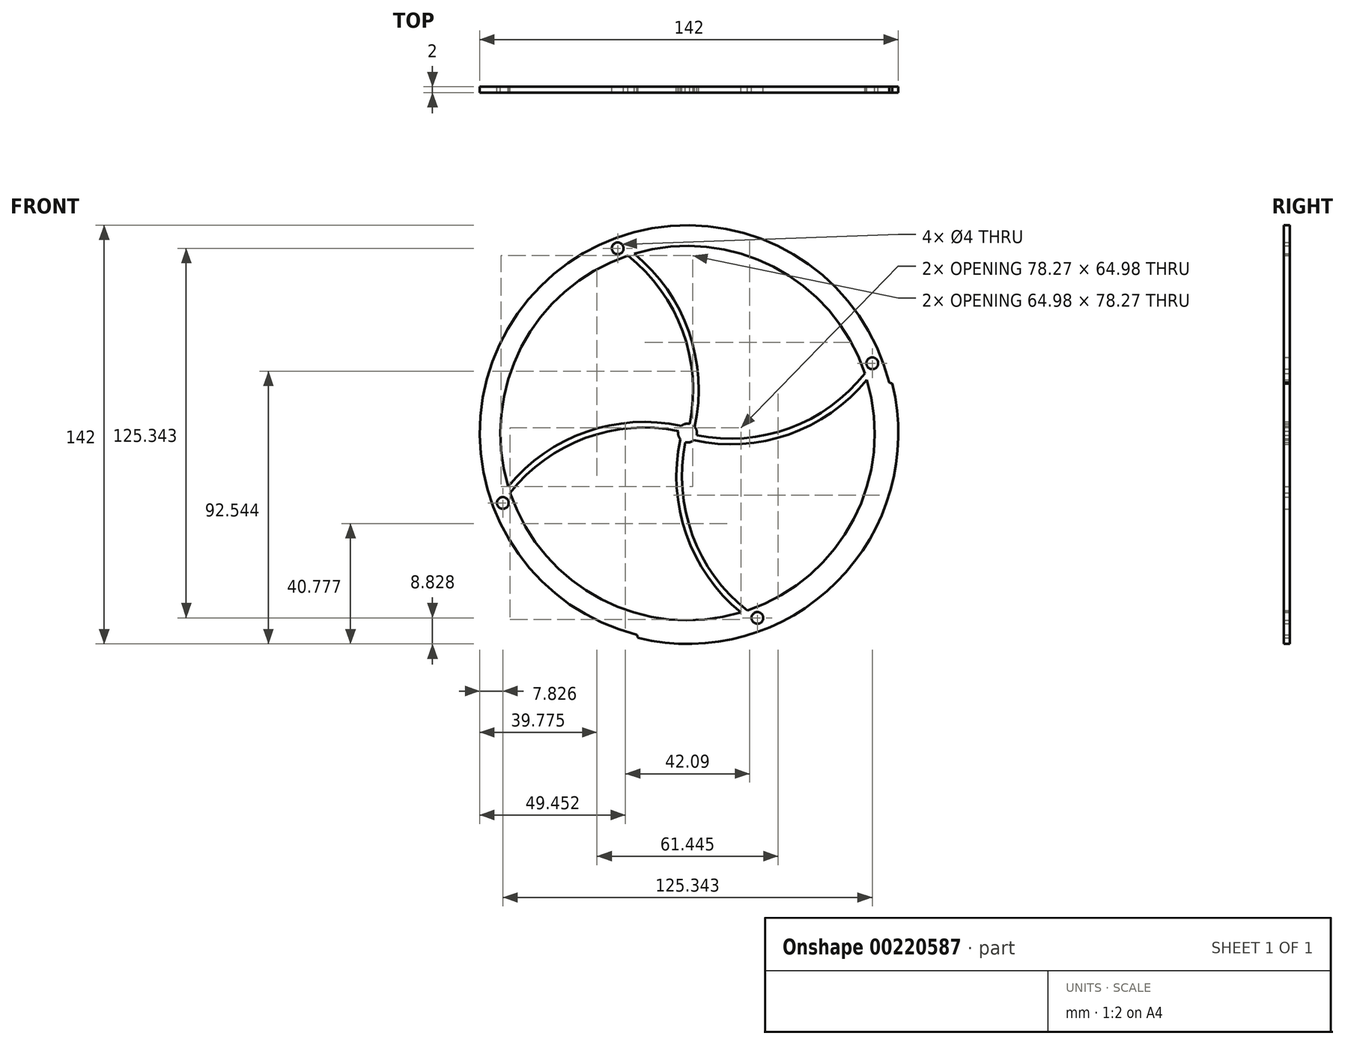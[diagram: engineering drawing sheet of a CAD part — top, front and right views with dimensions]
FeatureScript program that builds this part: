
annotation { "Feature Type Name" : "Feature", "Feature Type Description" : "" }
export const myFeature = defineFeature(function(context is Context, id is Id, definition is map)
    precondition{}
    {
        {
            var Q0;
            Q0=qCreatedBy(makeId("Front.planeOp"),FACE);
            var sketch = newSketch(context, id + "F0", { "sketchPlane" : qUnion([Q0])});
            skLineSegment(sketch, "E0.bottom", {"start": v(89.93, -111.44) * mm, "end": v(-110.07, -111.44) * mm});
            skLineSegment(sketch, "E0.top", {"start": v(89.93, 88.56) * mm, "end": v(-110.07, 88.56) * mm});
            skLineSegment(sketch, "E0.left", {"start": v(89.93, -111.44) * mm, "end": v(89.93, 88.56) * mm});
            skLineSegment(sketch, "E0.right", {"start": v(-110.07, -111.44) * mm, "end": v(-110.07, 88.56) * mm});
            skPoint(sketch, "E0.middle", {"position": v(-10.07, -11.44) * mm});
            skLineSegment(sketch, "E1", {"start": v(-110.07, 88.56) * mm, "end": v(89.93, -111.44) * mm, "construction": true});
            skLineSegment(sketch, "E2", {"start": v(89.93, 88.56) * mm, "end": v(-110.07, -111.44) * mm, "construction": true});
            skCircle(sketch, "E3", {"center": v(38.43, -59.95) * mm, "radius": 68.6 * mm});
            skCircle(sketch, "E4", {"center": v(38.6, 37.24) * mm, "radius": 68.84 * mm});
            skCircle(sketch, "E5", {"center": v(-16.12, 66.58) * mm, "radius": 6.75 * mm});
            skCircle(sketch, "E6", {"center": v(-10.07, -11.44) * mm, "radius": 71.5 * mm});
            skCircle(sketch, "E7", {"center": v(-16.12, 66.58) * mm, "radius": 2.5 * mm});
            skCircle(sketch, "E8", {"center": v(52.6, 12.25) * mm, "radius": 2.5 * mm});
            skCircle(sketch, "E9", {"center": v(62.37, 19.29) * mm, "radius": 2.5 * mm});
            skLineSegment(sketch, "E10", {"start": v(52.6, 12.25) * mm, "end": v(-33.76, 51.23) * mm, "construction": true});
            skLineSegment(sketch, "E11", {"start": v(-33.76, 51.23) * mm, "end": v(-72.74, -35.13) * mm, "construction": true});
            skLineSegment(sketch, "E12", {"start": v(-72.74, -35.13) * mm, "end": v(13.62, -74.11) * mm, "construction": true});
            skLineSegment(sketch, "E13", {"start": v(13.62, -74.11) * mm, "end": v(52.6, 12.25) * mm, "construction": true});
            skCircle(sketch, "E14", {"center": v(-10.07, -11.44) * mm, "radius": 67 * mm, "construction": true});
            skCircle(sketch, "E15", {"center": v(62.37, 19.29) * mm, "radius": 6.75 * mm, "construction": true});
            skArc(sketch, "E16", {"start": v(62.37, 19.29) * mm, "mid": v(30.57, 55.29) * mm, "end": v(-16.12, 66.58) * mm, "construction": true});
            skArc(sketch, "E17", {"start": v(60.01, 18.48) * mm, "mid": v(29.1, 53.19) * mm, "end": v(-16.1, 64.08) * mm});
            skArc(sketch, "E18", {"start": v(64.71, 20.17) * mm, "mid": v(31.98, 57.24) * mm, "end": v(-16.04, 69.07) * mm});
            skCircle(sketch, "E19", {"center": v(-33.76, 51.23) * mm, "radius": 2 * mm});
            skCircle(sketch, "E20", {"center": v(-72.74, -35.13) * mm, "radius": 2 * mm});
            skCircle(sketch, "E21", {"center": v(13.62, -74.11) * mm, "radius": 2 * mm});
            skCircle(sketch, "E22", {"center": v(52.6, 12.25) * mm, "radius": 2 * mm});
            skCircle(sketch, "E23", {"center": v(62.37, 19.29) * mm, "radius": 2 * mm});
            skCircle(sketch, "E24", {"center": v(-16.12, 66.58) * mm, "radius": 2 * mm});
            skArc(sketch, "E25", {"start": v(-10.07, -11.44) * mm, "mid": v(25.04, -9.58) * mm, "end": v(52.6, 12.25) * mm});
            skArc(sketch, "E26.0", {"start": v(-10.55, -13.28) * mm, "mid": v(25.7, -11.36) * mm, "end": v(54.17, 11.2) * mm});
            skLineSegment(sketch, "E27", {"start": v(-10.55, -13.28) * mm, "end": v(-10.07, -11.44) * mm});
            skLineSegment(sketch, "E28", {"start": v(52.6, 12.25) * mm, "end": v(54.17, 11.2) * mm});
            skArc(sketch, "E29.1.0", {"start": v(-8.23, -11.92) * mm, "mid": v(-10.15, 24.34) * mm, "end": v(-32.7, 52.8) * mm});
            skArc(sketch, "E29.1.1", {"start": v(-10.07, -11.44) * mm, "mid": v(-11.93, 23.67) * mm, "end": v(-33.76, 51.23) * mm});
            skLineSegment(sketch, "E29.1.2", {"start": v(-33.76, 51.23) * mm, "end": v(-32.7, 52.8) * mm});
            skLineSegment(sketch, "E29.1.3", {"start": v(-8.23, -11.92) * mm, "end": v(-10.07, -11.44) * mm});
            skArc(sketch, "E29.2.0", {"start": v(-9.6, -9.6) * mm, "mid": v(-45.86, -11.52) * mm, "end": v(-74.32, -34.07) * mm});
            skArc(sketch, "E29.2.1", {"start": v(-10.07, -11.44) * mm, "mid": v(-45.18, -13.3) * mm, "end": v(-72.74, -35.13) * mm});
            skLineSegment(sketch, "E29.2.2", {"start": v(-72.74, -35.13) * mm, "end": v(-74.32, -34.07) * mm});
            skLineSegment(sketch, "E29.2.3", {"start": v(-9.6, -9.6) * mm, "end": v(-10.07, -11.44) * mm});
            skArc(sketch, "E29.3.0", {"start": v(-11.91, -10.96) * mm, "mid": v(-10, -47.22) * mm, "end": v(12.56, -75.69) * mm});
            skArc(sketch, "E29.3.1", {"start": v(-10.07, -11.44) * mm, "mid": v(-8.21, -46.55) * mm, "end": v(13.62, -74.11) * mm});
            skLineSegment(sketch, "E29.3.2", {"start": v(13.62, -74.11) * mm, "end": v(12.56, -75.69) * mm});
            skLineSegment(sketch, "E29.3.3", {"start": v(-11.91, -10.96) * mm, "end": v(-10.07, -11.44) * mm});
            skCircle(sketch, "E30", {"center": v(-10.07, -11.44) * mm, "radius": 3.21 * mm});
            skCircle(sketch, "E31", {"center": v(-72.74, -35.13) * mm, "radius": 3 * mm});
            skCircle(sketch, "E32", {"center": v(-33.76, 51.23) * mm, "radius": 3 * mm});
            skCircle(sketch, "E33", {"center": v(52.6, 12.25) * mm, "radius": 3 * mm});
            skCircle(sketch, "E34", {"center": v(13.62, -74.11) * mm, "radius": 3 * mm});
            skCircle(sketch, "E35.0", {"center": v(-10.07, -11.44) * mm, "radius": 70.5 * mm});
            skCircle(sketch, "E36.0", {"center": v(-10.07, -11.44) * mm, "radius": 72 * mm});
            skCircle(sketch, "E37.0", {"center": v(-10.07, -11.44) * mm, "radius": 63.5 * mm});
            skCircle(sketch, "E38.0", {"center": v(-10.07, -11.44) * mm, "radius": 72 * mm, "construction": true});
            skSolve(sketch);
        }
        {
            var Q0;
            {var subQ0=sQuery(id+"F0.wireOp",EDGE,"E29.1.3");Q0=makeQuery(id+"F0.imprint","IMPRINT",FACE,{"disambiguationData":[TD([[makeQuery(id+"F0.imprint","IMPRINT",EDGE,{"derivedFrom":subQ0}),1.0]])]});}
            var Q1;
            {var subQ0=sQuery(id+"F0.wireOp",EDGE,"E25");var subQ5=sQuery(id+"F0.wireOp",EDGE,"E29.1.0");var subQ6=makeQuery(id+"F0.imprint","INTERSECT",VERTEX,{"derivedFrom":[subQ0,subQ5]});Q1=makeQuery(id+"F0.imprint","IMPRINT",FACE,{"disambiguationData":[TD([[makeQuery(id+"F0.imprint","IMPRINT",EDGE,{"disambiguationData":[TD([[subQ6,-1.0]])],"derivedFrom":subQ5}),1.0]])]});}
            var Q2;
            {var subQ0=sQuery(id+"F0.wireOp",EDGE,"E29.1.0");var subQ1=sQuery(id+"F0.wireOp",EDGE,"E25");var subQ2=makeQuery(id+"F0.imprint","INTERSECT",VERTEX,{"derivedFrom":[subQ1,subQ0]});Q2=makeQuery(id+"F0.imprint","IMPRINT",FACE,{"disambiguationData":[TD([[makeQuery(id+"F0.imprint","IMPRINT",EDGE,{"disambiguationData":[TD([[subQ2,-1.0]])],"derivedFrom":subQ1}),1.0]])]});}
            var Q3;
            {var subQ0=sQuery(id+"F0.wireOp",EDGE,"E29.1.3");Q3=makeQuery(id+"F0.imprint","IMPRINT",FACE,{"disambiguationData":[TD([[makeQuery(id+"F0.imprint","IMPRINT",EDGE,{"derivedFrom":subQ0}),-1.0]])]});}
            var Q4;
            {var subQ0=sQuery(id+"F0.wireOp",EDGE,"E29.3.1");var subQ5=sQuery(id+"F0.wireOp",EDGE,"E26.0");var subQ6=makeQuery(id+"F0.imprint","INTERSECT",VERTEX,{"derivedFrom":[subQ5,subQ0]});Q4=makeQuery(id+"F0.imprint","IMPRINT",FACE,{"disambiguationData":[TD([[makeQuery(id+"F0.imprint","IMPRINT",EDGE,{"disambiguationData":[TD([[subQ6,-1.0]])],"derivedFrom":subQ5}),1.0]])]});}
            var Q5;
            {var subQ0=sQuery(id+"F0.wireOp",EDGE,"E29.2.3");Q5=makeQuery(id+"F0.imprint","IMPRINT",FACE,{"disambiguationData":[TD([[makeQuery(id+"F0.imprint","IMPRINT",EDGE,{"derivedFrom":subQ0}),1.0]])]});}
            var Q6;
            {var subQ0=sQuery(id+"F0.wireOp",EDGE,"E29.1.1");var subQ5=sQuery(id+"F0.wireOp",EDGE,"E29.2.0");var subQ6=makeQuery(id+"F0.imprint","INTERSECT",VERTEX,{"derivedFrom":[subQ0,subQ5]});Q6=makeQuery(id+"F0.imprint","IMPRINT",FACE,{"disambiguationData":[TD([[makeQuery(id+"F0.imprint","IMPRINT",EDGE,{"disambiguationData":[TD([[subQ6,-1.0]])],"derivedFrom":subQ5}),1.0]])]});}
            var Q7;
            {var subQ0=sQuery(id+"F0.wireOp",EDGE,"E29.3.3");Q7=makeQuery(id+"F0.imprint","IMPRINT",FACE,{"disambiguationData":[TD([[makeQuery(id+"F0.imprint","IMPRINT",EDGE,{"derivedFrom":subQ0}),1.0]])]});}
            var Q8;
            {var subQ0=sQuery(id+"F0.wireOp",EDGE,"E29.2.1");var subQ5=sQuery(id+"F0.wireOp",EDGE,"E29.3.0");var subQ6=makeQuery(id+"F0.imprint","INTERSECT",VERTEX,{"derivedFrom":[subQ0,subQ5]});Q8=makeQuery(id+"F0.imprint","IMPRINT",FACE,{"disambiguationData":[TD([[makeQuery(id+"F0.imprint","IMPRINT",EDGE,{"disambiguationData":[TD([[subQ6,-1.0]])],"derivedFrom":subQ5}),1.0]])]});}
            var Q9;
            {var subQ0=sQuery(id+"F0.wireOp",EDGE,"E27");Q9=makeQuery(id+"F0.imprint","IMPRINT",FACE,{"disambiguationData":[TD([[makeQuery(id+"F0.imprint","IMPRINT",EDGE,{"derivedFrom":subQ0}),1.0]])]});}
            var Q10;
            {var subQ0=sQuery(id+"F0.wireOp",EDGE,"E29.3.1");var subQ1=sQuery(id+"F0.wireOp",EDGE,"E26.0");var subQ2=makeQuery(id+"F0.imprint","INTERSECT",VERTEX,{"derivedFrom":[subQ1,subQ0]});Q10=makeQuery(id+"F0.imprint","IMPRINT",FACE,{"disambiguationData":[TD([[makeQuery(id+"F0.imprint","IMPRINT",EDGE,{"disambiguationData":[TD([[subQ2,-1.0]])],"derivedFrom":subQ1}),-1.0]])]});}
            var Q11;
            {var subQ0=sQuery(id+"F0.wireOp",EDGE,"E29.2.0");var subQ1=sQuery(id+"F0.wireOp",EDGE,"E29.1.1");var subQ2=makeQuery(id+"F0.imprint","INTERSECT",VERTEX,{"derivedFrom":[subQ1,subQ0]});Q11=makeQuery(id+"F0.imprint","IMPRINT",FACE,{"disambiguationData":[TD([[makeQuery(id+"F0.imprint","IMPRINT",EDGE,{"disambiguationData":[TD([[subQ2,-1.0]])],"derivedFrom":subQ1}),1.0]])]});}
            var Q12;
            {var subQ0=sQuery(id+"F0.wireOp",EDGE,"E29.2.3");Q12=makeQuery(id+"F0.imprint","IMPRINT",FACE,{"disambiguationData":[TD([[makeQuery(id+"F0.imprint","IMPRINT",EDGE,{"derivedFrom":subQ0}),-1.0]])]});}
            var Q13;
            {var subQ0=sQuery(id+"F0.wireOp",EDGE,"E27");Q13=makeQuery(id+"F0.imprint","IMPRINT",FACE,{"disambiguationData":[TD([[makeQuery(id+"F0.imprint","IMPRINT",EDGE,{"derivedFrom":subQ0}),-1.0]])]});}
            var Q14;
            {var subQ0=sQuery(id+"F0.wireOp",EDGE,"E29.3.0");var subQ1=sQuery(id+"F0.wireOp",EDGE,"E29.2.1");var subQ2=makeQuery(id+"F0.imprint","INTERSECT",VERTEX,{"derivedFrom":[subQ1,subQ0]});Q14=makeQuery(id+"F0.imprint","IMPRINT",FACE,{"disambiguationData":[TD([[makeQuery(id+"F0.imprint","IMPRINT",EDGE,{"disambiguationData":[TD([[subQ2,-1.0]])],"derivedFrom":subQ1}),1.0]])]});}
            var Q15;
            {var subQ0=sQuery(id+"F0.wireOp",EDGE,"E29.3.3");Q15=makeQuery(id+"F0.imprint","IMPRINT",FACE,{"disambiguationData":[TD([[makeQuery(id+"F0.imprint","IMPRINT",EDGE,{"derivedFrom":subQ0}),-1.0]])]});}
            var Q16;
            {var subQ0=sQuery(id+"F0.wireOp",EDGE,"E26.0");var subQ1=sQuery(id+"F0.wireOp",EDGE,"E3");var subQ2=makeQuery(id+"F0.imprint","INTERSECT",VERTEX,{"derivedFrom":[subQ1,subQ0]});Q16=makeQuery(id+"F0.imprint","IMPRINT",FACE,{"disambiguationData":[TD([[makeQuery(id+"F0.imprint","IMPRINT",EDGE,{"disambiguationData":[TD([[subQ2,-1.0]])],"derivedFrom":subQ1}),1.0]])]});}
            var Q17;
            {var subQ0=sQuery(id+"F0.wireOp",EDGE,"E29.1.0");var subQ7=sQuery(id+"F0.wireOp",EDGE,"E3");var subQ8=makeQuery(id+"F0.imprint","INTERSECT",VERTEX,{"derivedFrom":[subQ7,subQ0]});Q17=makeQuery(id+"F0.imprint","IMPRINT",FACE,{"disambiguationData":[TD([[makeQuery(id+"F0.imprint","IMPRINT",EDGE,{"disambiguationData":[TD([[subQ8,-1.0]])],"derivedFrom":subQ7}),-1.0]])]});}
            var Q18;
            {var subQ5=sQuery(id+"F0.wireOp",EDGE,"E29.2.0");var subQ6=sQuery(id+"F0.wireOp",EDGE,"E4");var subQ7=makeQuery(id+"F0.imprint","INTERSECT",VERTEX,{"derivedFrom":[subQ6,subQ5]});Q18=makeQuery(id+"F0.imprint","IMPRINT",FACE,{"disambiguationData":[TD([[makeQuery(id+"F0.imprint","IMPRINT",EDGE,{"disambiguationData":[TD([[subQ7,-1.0]])],"derivedFrom":subQ6}),-1.0]])]});}
            var Q19;
            {var subQ1=sQuery(id+"F0.wireOp",EDGE,"E3");var subQ7=sQuery(id+"F0.wireOp",EDGE,"E30");var subQ9=makeQuery(id+"F0.imprint","INTERSECT",VERTEX,{"disambiguationData":[OD(1.0)],"derivedFrom":[subQ1,subQ7]});Q19=makeQuery(id+"F0.imprint","IMPRINT",FACE,{"disambiguationData":[TD([[makeQuery(id+"F0.imprint","IMPRINT",EDGE,{"disambiguationData":[TD([[subQ9,-1.0]])],"derivedFrom":subQ1}),1.0]])]});}
            var Q20;
            {var subQ0=sQuery(id+"F0.wireOp",EDGE,"E30");var subQ1=sQuery(id+"F0.wireOp",EDGE,"E3");var subQ2=makeQuery(id+"F0.imprint","INTERSECT",VERTEX,{"disambiguationData":[OD(1.0)],"derivedFrom":[subQ1,subQ0]});Q20=makeQuery(id+"F0.imprint","IMPRINT",FACE,{"disambiguationData":[TD([[makeQuery(id+"F0.imprint","IMPRINT",EDGE,{"disambiguationData":[TD([[subQ2,-1.0]])],"derivedFrom":subQ1}),-1.0]])]});}
            var Q21;
            {var subQ0=sQuery(id+"F0.wireOp",EDGE,"E30");var subQ1=sQuery(id+"F0.wireOp",EDGE,"E4");var subQ2=makeQuery(id+"F0.imprint","INTERSECT",VERTEX,{"disambiguationData":[OD(1.0)],"derivedFrom":[subQ1,subQ0]});Q21=makeQuery(id+"F0.imprint","IMPRINT",FACE,{"disambiguationData":[TD([[makeQuery(id+"F0.imprint","IMPRINT",EDGE,{"disambiguationData":[TD([[subQ2,-1.0]])],"derivedFrom":subQ1}),-1.0]])]});}
            var Q22;
            {var subQ0=sQuery(id+"F0.wireOp",EDGE,"E29.2.0");var subQ1=sQuery(id+"F0.wireOp",EDGE,"E4");var subQ2=makeQuery(id+"F0.imprint","INTERSECT",VERTEX,{"derivedFrom":[subQ1,subQ0]});Q22=makeQuery(id+"F0.imprint","IMPRINT",FACE,{"disambiguationData":[TD([[makeQuery(id+"F0.imprint","IMPRINT",EDGE,{"disambiguationData":[TD([[subQ2,-1.0]])],"derivedFrom":subQ1}),1.0]])]});}
            var Q23;
            {var subQ0=sQuery(id+"F0.wireOp",EDGE,"E29.1.0");var subQ1=sQuery(id+"F0.wireOp",EDGE,"E3");var subQ2=makeQuery(id+"F0.imprint","INTERSECT",VERTEX,{"derivedFrom":[subQ1,subQ0]});Q23=makeQuery(id+"F0.imprint","IMPRINT",FACE,{"disambiguationData":[TD([[makeQuery(id+"F0.imprint","IMPRINT",EDGE,{"disambiguationData":[TD([[subQ2,-1.0]])],"derivedFrom":subQ1}),1.0]])]});}
            var Q24;
            {var subQ0=sQuery(id+"F0.wireOp",EDGE,"E26.0");var subQ1=sQuery(id+"F0.wireOp",EDGE,"E3");var subQ2=makeQuery(id+"F0.imprint","INTERSECT",VERTEX,{"derivedFrom":[subQ1,subQ0]});Q24=makeQuery(id+"F0.imprint","IMPRINT",FACE,{"disambiguationData":[TD([[makeQuery(id+"F0.imprint","IMPRINT",EDGE,{"disambiguationData":[TD([[subQ2,-1.0]])],"derivedFrom":subQ1}),-1.0]])]});}
            var Q25;
            {var subQ0=sQuery(id+"F0.wireOp",EDGE,"E29.1.0");var subQ1=sQuery(id+"F0.wireOp",EDGE,"E4");var subQ2=makeQuery(id+"F0.imprint","INTERSECT",VERTEX,{"derivedFrom":[subQ1,subQ0]});Q25=makeQuery(id+"F0.imprint","IMPRINT",FACE,{"disambiguationData":[TD([[makeQuery(id+"F0.imprint","IMPRINT",EDGE,{"disambiguationData":[TD([[subQ2,-1.0]])],"derivedFrom":subQ1}),-1.0]])]});}
            var Q26;
            {var subQ0=sQuery(id+"F0.wireOp",EDGE,"E29.2.0");var subQ1=sQuery(id+"F0.wireOp",EDGE,"E20");var subQ2=makeQuery(id+"F0.imprint","INTERSECT",VERTEX,{"derivedFrom":[subQ1,subQ0]});Q26=makeQuery(id+"F0.imprint","IMPRINT",FACE,{"disambiguationData":[TD([[makeQuery(id+"F0.imprint","IMPRINT",EDGE,{"disambiguationData":[TD([[subQ2,1.0]])],"derivedFrom":subQ1}),-1.0]])]});}
            var Q27;
            {var subQ0=sQuery(id+"F0.wireOp",EDGE,"E29.2.0");var subQ1=sQuery(id+"F0.wireOp",EDGE,"E20");var subQ2=makeQuery(id+"F0.imprint","INTERSECT",VERTEX,{"derivedFrom":[subQ1,subQ0]});Q27=makeQuery(id+"F0.imprint","IMPRINT",FACE,{"disambiguationData":[TD([[makeQuery(id+"F0.imprint","IMPRINT",EDGE,{"disambiguationData":[TD([[subQ2,-1.0]])],"derivedFrom":subQ1}),-1.0]])]});}
            var Q28;
            {var subQ0=sQuery(id+"F0.wireOp",EDGE,"E29.3.0");var subQ1=sQuery(id+"F0.wireOp",EDGE,"E21");var subQ2=makeQuery(id+"F0.imprint","INTERSECT",VERTEX,{"derivedFrom":[subQ1,subQ0]});Q28=makeQuery(id+"F0.imprint","IMPRINT",FACE,{"disambiguationData":[TD([[makeQuery(id+"F0.imprint","IMPRINT",EDGE,{"disambiguationData":[TD([[subQ2,-1.0]])],"derivedFrom":subQ1}),-1.0]])]});}
            var Q29;
            {var subQ0=sQuery(id+"F0.wireOp",EDGE,"E29.3.0");var subQ1=sQuery(id+"F0.wireOp",EDGE,"E21");var subQ2=makeQuery(id+"F0.imprint","INTERSECT",VERTEX,{"derivedFrom":[subQ1,subQ0]});Q29=makeQuery(id+"F0.imprint","IMPRINT",FACE,{"disambiguationData":[TD([[makeQuery(id+"F0.imprint","IMPRINT",EDGE,{"disambiguationData":[TD([[subQ2,1.0]])],"derivedFrom":subQ1}),-1.0]])]});}
            var Q30;
            {var subQ0=sQuery(id+"F0.wireOp",EDGE,"E29.1.0");var subQ1=sQuery(id+"F0.wireOp",EDGE,"E19");var subQ2=makeQuery(id+"F0.imprint","INTERSECT",VERTEX,{"derivedFrom":[subQ1,subQ0]});Q30=makeQuery(id+"F0.imprint","IMPRINT",FACE,{"disambiguationData":[TD([[makeQuery(id+"F0.imprint","IMPRINT",EDGE,{"disambiguationData":[TD([[subQ2,-1.0]])],"derivedFrom":subQ1}),-1.0]])]});}
            var Q31;
            {var subQ0=sQuery(id+"F0.wireOp",EDGE,"E29.1.0");var subQ1=sQuery(id+"F0.wireOp",EDGE,"E19");var subQ2=makeQuery(id+"F0.imprint","INTERSECT",VERTEX,{"derivedFrom":[subQ1,subQ0]});Q31=makeQuery(id+"F0.imprint","IMPRINT",FACE,{"disambiguationData":[TD([[makeQuery(id+"F0.imprint","IMPRINT",EDGE,{"disambiguationData":[TD([[subQ2,1.0]])],"derivedFrom":subQ1}),-1.0]])]});}
            var Q32;
            {var subQ0=sQuery(id+"F0.wireOp",EDGE,"E25");var subQ1=sQuery(id+"F0.wireOp",EDGE,"E8");var subQ2=makeQuery(id+"F0.imprint","INTERSECT",VERTEX,{"derivedFrom":[subQ1,subQ0]});Q32=makeQuery(id+"F0.imprint","IMPRINT",FACE,{"disambiguationData":[TD([[makeQuery(id+"F0.imprint","IMPRINT",EDGE,{"disambiguationData":[TD([[subQ2,1.0]])],"derivedFrom":subQ1}),-1.0]])]});}
            var Q33;
            {var subQ0=sQuery(id+"F0.wireOp",EDGE,"E25");var subQ1=sQuery(id+"F0.wireOp",EDGE,"E8");var subQ2=makeQuery(id+"F0.imprint","INTERSECT",VERTEX,{"derivedFrom":[subQ1,subQ0]});Q33=makeQuery(id+"F0.imprint","IMPRINT",FACE,{"disambiguationData":[TD([[makeQuery(id+"F0.imprint","IMPRINT",EDGE,{"disambiguationData":[TD([[subQ2,1.0]])],"derivedFrom":subQ1}),1.0]])]});}
            var Q34;
            {var subQ0=sQuery(id+"F0.wireOp",EDGE,"E25");var subQ1=sQuery(id+"F0.wireOp",EDGE,"E8");var subQ2=makeQuery(id+"F0.imprint","INTERSECT",VERTEX,{"derivedFrom":[subQ1,subQ0]});Q34=makeQuery(id+"F0.imprint","IMPRINT",FACE,{"disambiguationData":[TD([[makeQuery(id+"F0.imprint","IMPRINT",EDGE,{"disambiguationData":[TD([[subQ2,-1.0]])],"derivedFrom":subQ1}),-1.0]])]});}
            var Q35;
            {var subQ0=sQuery(id+"F0.wireOp",EDGE,"E25");var subQ1=sQuery(id+"F0.wireOp",EDGE,"E8");var subQ2=makeQuery(id+"F0.imprint","INTERSECT",VERTEX,{"derivedFrom":[subQ1,subQ0]});Q35=makeQuery(id+"F0.imprint","IMPRINT",FACE,{"disambiguationData":[TD([[makeQuery(id+"F0.imprint","IMPRINT",EDGE,{"disambiguationData":[TD([[subQ2,-1.0]])],"derivedFrom":subQ1}),1.0]])]});}
            var Q36;
            {var subQ5=sQuery(id+"F0.wireOp",EDGE,"E37.0");var subQ7=sQuery(id+"F0.wireOp",EDGE,"E29.2.0");var subQ9=makeQuery(id+"F0.imprint","INTERSECT",VERTEX,{"derivedFrom":[subQ7,subQ5]});Q36=makeQuery(id+"F0.imprint","IMPRINT",FACE,{"disambiguationData":[TD([[makeQuery(id+"F0.imprint","IMPRINT",EDGE,{"disambiguationData":[TD([[subQ9,-1.0]])],"derivedFrom":subQ7}),-1.0]])]});}
            var Q37;
            {var subQ0=sQuery(id+"F0.wireOp",EDGE,"E35.0");var subQ1=sQuery(id+"F0.wireOp",EDGE,"E19");var subQ2=makeQuery(id+"F0.imprint","INTERSECT",VERTEX,{"derivedFrom":[subQ1,subQ0]});Q37=makeQuery(id+"F0.imprint","IMPRINT",FACE,{"disambiguationData":[TD([[makeQuery(id+"F0.imprint","IMPRINT",EDGE,{"disambiguationData":[TD([[subQ2,-1.0]])],"derivedFrom":subQ1}),-1.0]])]});}
            var Q38;
            {var subQ0=sQuery(id+"F0.wireOp",EDGE,"E35.0");var subQ1=sQuery(id+"F0.wireOp",EDGE,"E32");var subQ2=makeQuery(id+"F0.imprint","INTERSECT",VERTEX,{"disambiguationData":[OD(0.0)],"derivedFrom":[subQ1,subQ0]});Q38=makeQuery(id+"F0.imprint","IMPRINT",FACE,{"disambiguationData":[TD([[makeQuery(id+"F0.imprint","IMPRINT",EDGE,{"disambiguationData":[TD([[subQ2,-1.0]])],"derivedFrom":subQ1}),1.0]])]});}
            var Q39;
            {var subQ0=sQuery(id+"F0.wireOp",EDGE,"E32");var subQ1=sQuery(id+"F0.wireOp",EDGE,"E29.1.1");var subQ2=makeQuery(id+"F0.imprint","INTERSECT",VERTEX,{"derivedFrom":[subQ1,subQ0]});Q39=makeQuery(id+"F0.imprint","IMPRINT",FACE,{"disambiguationData":[TD([[makeQuery(id+"F0.imprint","IMPRINT",EDGE,{"disambiguationData":[TD([[subQ2,-1.0]])],"derivedFrom":subQ1}),1.0]])]});}
            var Q40;
            {var subQ0=sQuery(id+"F0.wireOp",EDGE,"E32");var subQ1=sQuery(id+"F0.wireOp",EDGE,"E29.1.1");var subQ2=makeQuery(id+"F0.imprint","INTERSECT",VERTEX,{"derivedFrom":[subQ1,subQ0]});Q40=makeQuery(id+"F0.imprint","IMPRINT",FACE,{"disambiguationData":[TD([[makeQuery(id+"F0.imprint","IMPRINT",EDGE,{"disambiguationData":[TD([[subQ2,-1.0]])],"derivedFrom":subQ1}),-1.0]])]});}
            var Q41;
            {var subQ0=sQuery(id+"F0.wireOp",EDGE,"E37.0");var subQ1=sQuery(id+"F0.wireOp",EDGE,"E19");var subQ2=makeQuery(id+"F0.imprint","INTERSECT",VERTEX,{"derivedFrom":[subQ1,subQ0]});Q41=makeQuery(id+"F0.imprint","IMPRINT",FACE,{"disambiguationData":[TD([[makeQuery(id+"F0.imprint","IMPRINT",EDGE,{"disambiguationData":[TD([[subQ2,-1.0]])],"derivedFrom":subQ1}),-1.0]])]});}
            var Q42;
            {var subQ0=sQuery(id+"F0.wireOp",EDGE,"E37.0");var subQ1=sQuery(id+"F0.wireOp",EDGE,"E29.1.0");var subQ2=makeQuery(id+"F0.imprint","INTERSECT",VERTEX,{"derivedFrom":[subQ1,subQ0]});Q42=makeQuery(id+"F0.imprint","IMPRINT",FACE,{"disambiguationData":[TD([[makeQuery(id+"F0.imprint","IMPRINT",EDGE,{"disambiguationData":[TD([[subQ2,-1.0]])],"derivedFrom":subQ1}),1.0]])]});}
            var Q43;
            {var subQ0=sQuery(id+"F0.wireOp",EDGE,"E35.0");var subQ1=sQuery(id+"F0.wireOp",EDGE,"E4");var subQ2=makeQuery(id+"F0.imprint","INTERSECT",VERTEX,{"disambiguationData":[OD(0.0)],"derivedFrom":[subQ1,subQ0]});Q43=makeQuery(id+"F0.imprint","IMPRINT",FACE,{"disambiguationData":[TD([[makeQuery(id+"F0.imprint","IMPRINT",EDGE,{"disambiguationData":[TD([[subQ2,-1.0]])],"derivedFrom":subQ1}),1.0]])]});}
            var Q44;
            {var subQ3=sQuery(id+"F0.wireOp",EDGE,"E35.0");var subQ7=sQuery(id+"F0.wireOp",EDGE,"E4");var subQ9=makeQuery(id+"F0.imprint","INTERSECT",VERTEX,{"disambiguationData":[OD(0.0)],"derivedFrom":[subQ7,subQ3]});Q44=makeQuery(id+"F0.imprint","IMPRINT",FACE,{"disambiguationData":[TD([[makeQuery(id+"F0.imprint","IMPRINT",EDGE,{"disambiguationData":[TD([[subQ9,-1.0]])],"derivedFrom":subQ7}),-1.0]])]});}
            var Q45;
            {var subQ0=sQuery(id+"F0.wireOp",EDGE,"E35.0");var subQ1=sQuery(id+"F0.wireOp",EDGE,"E34");var subQ2=makeQuery(id+"F0.imprint","INTERSECT",VERTEX,{"disambiguationData":[OD(0.0)],"derivedFrom":[subQ1,subQ0]});Q45=makeQuery(id+"F0.imprint","IMPRINT",FACE,{"disambiguationData":[TD([[makeQuery(id+"F0.imprint","IMPRINT",EDGE,{"disambiguationData":[TD([[subQ2,-1.0]])],"derivedFrom":subQ1}),1.0]])]});}
            var Q46;
            {var subQ0=sQuery(id+"F0.wireOp",EDGE,"E34");var subQ1=sQuery(id+"F0.wireOp",EDGE,"E29.3.1");var subQ2=makeQuery(id+"F0.imprint","INTERSECT",VERTEX,{"derivedFrom":[subQ1,subQ0]});Q46=makeQuery(id+"F0.imprint","IMPRINT",FACE,{"disambiguationData":[TD([[makeQuery(id+"F0.imprint","IMPRINT",EDGE,{"disambiguationData":[TD([[subQ2,-1.0]])],"derivedFrom":subQ1}),1.0]])]});}
            var Q47;
            {var subQ0=sQuery(id+"F0.wireOp",EDGE,"E29.3.1");var subQ1=sQuery(id+"F0.wireOp",EDGE,"E21");var subQ2=makeQuery(id+"F0.imprint","INTERSECT",VERTEX,{"derivedFrom":[subQ1,subQ0]});Q47=makeQuery(id+"F0.imprint","IMPRINT",FACE,{"disambiguationData":[TD([[makeQuery(id+"F0.imprint","IMPRINT",EDGE,{"disambiguationData":[TD([[subQ2,1.0]])],"derivedFrom":subQ1}),-1.0]])]});}
            var Q48;
            {var subQ0=sQuery(id+"F0.wireOp",EDGE,"E34");var subQ1=sQuery(id+"F0.wireOp",EDGE,"E29.3.1");var subQ2=makeQuery(id+"F0.imprint","INTERSECT",VERTEX,{"derivedFrom":[subQ1,subQ0]});Q48=makeQuery(id+"F0.imprint","IMPRINT",FACE,{"disambiguationData":[TD([[makeQuery(id+"F0.imprint","IMPRINT",EDGE,{"disambiguationData":[TD([[subQ2,-1.0]])],"derivedFrom":subQ1}),-1.0]])]});}
            var Q49;
            {var subQ0=sQuery(id+"F0.wireOp",EDGE,"E37.0");var subQ1=sQuery(id+"F0.wireOp",EDGE,"E29.3.0");var subQ2=makeQuery(id+"F0.imprint","INTERSECT",VERTEX,{"derivedFrom":[subQ1,subQ0]});Q49=makeQuery(id+"F0.imprint","IMPRINT",FACE,{"disambiguationData":[TD([[makeQuery(id+"F0.imprint","IMPRINT",EDGE,{"disambiguationData":[TD([[subQ2,-1.0]])],"derivedFrom":subQ1}),1.0]])]});}
            var Q50;
            {var subQ0=sQuery(id+"F0.wireOp",EDGE,"E37.0");var subQ1=sQuery(id+"F0.wireOp",EDGE,"E21");var subQ2=makeQuery(id+"F0.imprint","INTERSECT",VERTEX,{"derivedFrom":[subQ1,subQ0]});Q50=makeQuery(id+"F0.imprint","IMPRINT",FACE,{"disambiguationData":[TD([[makeQuery(id+"F0.imprint","IMPRINT",EDGE,{"disambiguationData":[TD([[subQ2,1.0]])],"derivedFrom":subQ1}),-1.0]])]});}
            var Q51;
            {var subQ0=sQuery(id+"F0.wireOp",EDGE,"E37.0");var subQ1=sQuery(id+"F0.wireOp",EDGE,"E4");var subQ2=makeQuery(id+"F0.imprint","INTERSECT",VERTEX,{"disambiguationData":[OD(1.0)],"derivedFrom":[subQ1,subQ0]});Q51=makeQuery(id+"F0.imprint","IMPRINT",FACE,{"disambiguationData":[TD([[makeQuery(id+"F0.imprint","IMPRINT",EDGE,{"disambiguationData":[TD([[subQ2,-1.0]])],"derivedFrom":subQ1}),-1.0]])]});}
            var Q52;
            {var subQ5=sQuery(id+"F0.wireOp",EDGE,"E37.0");var subQ7=sQuery(id+"F0.wireOp",EDGE,"E3");var subQ9=makeQuery(id+"F0.imprint","INTERSECT",VERTEX,{"disambiguationData":[OD(1.0)],"derivedFrom":[subQ7,subQ5]});Q52=makeQuery(id+"F0.imprint","IMPRINT",FACE,{"disambiguationData":[TD([[makeQuery(id+"F0.imprint","IMPRINT",EDGE,{"disambiguationData":[TD([[subQ9,-1.0]])],"derivedFrom":subQ7}),1.0]])]});}
            var Q53;
            {var subQ0=sQuery(id+"F0.wireOp",EDGE,"E35.0");var subQ1=sQuery(id+"F0.wireOp",EDGE,"E31");var subQ2=makeQuery(id+"F0.imprint","INTERSECT",VERTEX,{"disambiguationData":[OD(0.0)],"derivedFrom":[subQ1,subQ0]});Q53=makeQuery(id+"F0.imprint","IMPRINT",FACE,{"disambiguationData":[TD([[makeQuery(id+"F0.imprint","IMPRINT",EDGE,{"disambiguationData":[TD([[subQ2,-1.0]])],"derivedFrom":subQ1}),1.0]])]});}
            var Q54;
            {var subQ0=sQuery(id+"F0.wireOp",EDGE,"E31");var subQ1=sQuery(id+"F0.wireOp",EDGE,"E29.2.1");var subQ2=makeQuery(id+"F0.imprint","INTERSECT",VERTEX,{"derivedFrom":[subQ1,subQ0]});Q54=makeQuery(id+"F0.imprint","IMPRINT",FACE,{"disambiguationData":[TD([[makeQuery(id+"F0.imprint","IMPRINT",EDGE,{"disambiguationData":[TD([[subQ2,-1.0]])],"derivedFrom":subQ1}),1.0]])]});}
            var Q55;
            {var subQ0=sQuery(id+"F0.wireOp",EDGE,"E37.0");var subQ1=sQuery(id+"F0.wireOp",EDGE,"E3");var subQ2=makeQuery(id+"F0.imprint","INTERSECT",VERTEX,{"disambiguationData":[OD(1.0)],"derivedFrom":[subQ1,subQ0]});Q55=makeQuery(id+"F0.imprint","IMPRINT",FACE,{"disambiguationData":[TD([[makeQuery(id+"F0.imprint","IMPRINT",EDGE,{"disambiguationData":[TD([[subQ2,-1.0]])],"derivedFrom":subQ1}),-1.0]])]});}
            var Q56;
            {var subQ0=sQuery(id+"F0.wireOp",EDGE,"E37.0");var subQ1=sQuery(id+"F0.wireOp",EDGE,"E29.2.0");var subQ2=makeQuery(id+"F0.imprint","INTERSECT",VERTEX,{"derivedFrom":[subQ1,subQ0]});Q56=makeQuery(id+"F0.imprint","IMPRINT",FACE,{"disambiguationData":[TD([[makeQuery(id+"F0.imprint","IMPRINT",EDGE,{"disambiguationData":[TD([[subQ2,-1.0]])],"derivedFrom":subQ1}),1.0]])]});}
            var Q57;
            {var subQ0=sQuery(id+"F0.wireOp",EDGE,"E31");var subQ1=sQuery(id+"F0.wireOp",EDGE,"E29.2.1");var subQ2=makeQuery(id+"F0.imprint","INTERSECT",VERTEX,{"derivedFrom":[subQ1,subQ0]});Q57=makeQuery(id+"F0.imprint","IMPRINT",FACE,{"disambiguationData":[TD([[makeQuery(id+"F0.imprint","IMPRINT",EDGE,{"disambiguationData":[TD([[subQ2,-1.0]])],"derivedFrom":subQ1}),-1.0]])]});}
            var Q58;
            {var subQ0=sQuery(id+"F0.wireOp",EDGE,"E37.0");var subQ1=sQuery(id+"F0.wireOp",EDGE,"E20");var subQ2=makeQuery(id+"F0.imprint","INTERSECT",VERTEX,{"derivedFrom":[subQ1,subQ0]});Q58=makeQuery(id+"F0.imprint","IMPRINT",FACE,{"disambiguationData":[TD([[makeQuery(id+"F0.imprint","IMPRINT",EDGE,{"disambiguationData":[TD([[subQ2,1.0]])],"derivedFrom":subQ1}),-1.0]])]});}
            var Q59;
            {var subQ0=sQuery(id+"F0.wireOp",EDGE,"E35.0");var subQ1=sQuery(id+"F0.wireOp",EDGE,"E3");var subQ2=makeQuery(id+"F0.imprint","INTERSECT",VERTEX,{"disambiguationData":[OD(0.0)],"derivedFrom":[subQ1,subQ0]});Q59=makeQuery(id+"F0.imprint","IMPRINT",FACE,{"disambiguationData":[TD([[makeQuery(id+"F0.imprint","IMPRINT",EDGE,{"disambiguationData":[TD([[subQ2,-1.0]])],"derivedFrom":subQ1}),1.0]])]});}
            var Q60;
            {var subQ0=sQuery(id+"F0.wireOp",EDGE,"E37.0");var subQ1=sQuery(id+"F0.wireOp",EDGE,"E26.0");var subQ2=makeQuery(id+"F0.imprint","INTERSECT",VERTEX,{"derivedFrom":[subQ1,subQ0]});Q60=makeQuery(id+"F0.imprint","IMPRINT",FACE,{"disambiguationData":[TD([[makeQuery(id+"F0.imprint","IMPRINT",EDGE,{"disambiguationData":[TD([[subQ2,-1.0]])],"derivedFrom":subQ1}),1.0]])]});}
            var Q61;
            {var subQ0=sQuery(id+"F0.wireOp",EDGE,"E35.0");var subQ1=sQuery(id+"F0.wireOp",EDGE,"E3");var subQ2=makeQuery(id+"F0.imprint","INTERSECT",VERTEX,{"disambiguationData":[OD(0.0)],"derivedFrom":[subQ1,subQ0]});Q61=makeQuery(id+"F0.imprint","IMPRINT",FACE,{"disambiguationData":[TD([[makeQuery(id+"F0.imprint","IMPRINT",EDGE,{"disambiguationData":[TD([[subQ2,-1.0]])],"derivedFrom":subQ1}),-1.0]])]});}
            var Q62;
            {var subQ0=sQuery(id+"F0.wireOp",EDGE,"E37.0");var subQ1=sQuery(id+"F0.wireOp",EDGE,"E8");var subQ2=makeQuery(id+"F0.imprint","INTERSECT",VERTEX,{"disambiguationData":[OD(0.0)],"derivedFrom":[subQ1,subQ0]});Q62=makeQuery(id+"F0.imprint","IMPRINT",FACE,{"disambiguationData":[TD([[makeQuery(id+"F0.imprint","IMPRINT",EDGE,{"disambiguationData":[TD([[subQ2,1.0]])],"derivedFrom":subQ1}),-1.0]])]});}
            var Q63;
            {var subQ0=sQuery(id+"F0.wireOp",EDGE,"E35.0");var subQ1=sQuery(id+"F0.wireOp",EDGE,"E8");var subQ2=makeQuery(id+"F0.imprint","INTERSECT",VERTEX,{"disambiguationData":[OD(0.0)],"derivedFrom":[subQ1,subQ0]});Q63=makeQuery(id+"F0.imprint","IMPRINT",FACE,{"disambiguationData":[TD([[makeQuery(id+"F0.imprint","IMPRINT",EDGE,{"disambiguationData":[TD([[subQ2,1.0]])],"derivedFrom":subQ1}),1.0]])]});}
            var Q64;
            {var subQ0=sQuery(id+"F0.wireOp",EDGE,"E35.0");var subQ1=sQuery(id+"F0.wireOp",EDGE,"E8");var subQ2=makeQuery(id+"F0.imprint","INTERSECT",VERTEX,{"disambiguationData":[OD(0.0)],"derivedFrom":[subQ1,subQ0]});Q64=makeQuery(id+"F0.imprint","IMPRINT",FACE,{"disambiguationData":[TD([[makeQuery(id+"F0.imprint","IMPRINT",EDGE,{"disambiguationData":[TD([[subQ2,1.0]])],"derivedFrom":subQ1}),-1.0]])]});}
            var Q65;
            {var subQ0=sQuery(id+"F0.wireOp",EDGE,"E37.0");var subQ1=sQuery(id+"F0.wireOp",EDGE,"E8");var subQ2=makeQuery(id+"F0.imprint","INTERSECT",VERTEX,{"disambiguationData":[OD(0.0)],"derivedFrom":[subQ1,subQ0]});Q65=makeQuery(id+"F0.imprint","IMPRINT",FACE,{"disambiguationData":[TD([[makeQuery(id+"F0.imprint","IMPRINT",EDGE,{"disambiguationData":[TD([[subQ2,1.0]])],"derivedFrom":subQ1}),1.0]])]});}
            var Q66;
            {var subQ0=sQuery(id+"F0.wireOp",EDGE,"E26.0");var subQ1=sQuery(id+"F0.wireOp",EDGE,"E8");var subQ2=makeQuery(id+"F0.imprint","INTERSECT",VERTEX,{"derivedFrom":[subQ1,subQ0]});Q66=makeQuery(id+"F0.imprint","IMPRINT",FACE,{"disambiguationData":[TD([[makeQuery(id+"F0.imprint","IMPRINT",EDGE,{"disambiguationData":[TD([[subQ2,-1.0]])],"derivedFrom":subQ1}),1.0]])]});}
            var Q67;
            {var subQ0=sQuery(id+"F0.wireOp",EDGE,"E26.0");var subQ1=sQuery(id+"F0.wireOp",EDGE,"E8");var subQ2=makeQuery(id+"F0.imprint","INTERSECT",VERTEX,{"derivedFrom":[subQ1,subQ0]});Q67=makeQuery(id+"F0.imprint","IMPRINT",FACE,{"disambiguationData":[TD([[makeQuery(id+"F0.imprint","IMPRINT",EDGE,{"disambiguationData":[TD([[subQ2,-1.0]])],"derivedFrom":subQ1}),-1.0]])]});}
            var Q68;
            {var subQ0=sQuery(id+"F0.wireOp",EDGE,"E37.0");var subQ1=sQuery(id+"F0.wireOp",EDGE,"E8");var subQ2=makeQuery(id+"F0.imprint","INTERSECT",VERTEX,{"disambiguationData":[OD(1.0)],"derivedFrom":[subQ1,subQ0]});Q68=makeQuery(id+"F0.imprint","IMPRINT",FACE,{"disambiguationData":[TD([[makeQuery(id+"F0.imprint","IMPRINT",EDGE,{"disambiguationData":[TD([[subQ2,-1.0]])],"derivedFrom":subQ1}),-1.0]])]});}
            var Q69;
            {var subQ3=sQuery(id+"F0.wireOp",EDGE,"E37.0");var subQ7=sQuery(id+"F0.wireOp",EDGE,"E8");var subQ9=makeQuery(id+"F0.imprint","INTERSECT",VERTEX,{"disambiguationData":[OD(1.0)],"derivedFrom":[subQ7,subQ3]});Q69=makeQuery(id+"F0.imprint","IMPRINT",FACE,{"disambiguationData":[TD([[makeQuery(id+"F0.imprint","IMPRINT",EDGE,{"disambiguationData":[TD([[subQ9,-1.0]])],"derivedFrom":subQ7}),1.0]])]});}
            var Q70;
            {var subQ0=sQuery(id+"F0.wireOp",EDGE,"E37.0");var subQ1=sQuery(id+"F0.wireOp",EDGE,"E22");var subQ2=makeQuery(id+"F0.imprint","INTERSECT",VERTEX,{"derivedFrom":[subQ1,subQ0]});Q70=makeQuery(id+"F0.imprint","IMPRINT",FACE,{"disambiguationData":[TD([[makeQuery(id+"F0.imprint","IMPRINT",EDGE,{"disambiguationData":[TD([[subQ2,-1.0]])],"derivedFrom":subQ1}),-1.0]])]});}
            var Q71;
            {var subQ0=sQuery(id+"F0.wireOp",EDGE,"E29.2.1");var subQ1=sQuery(id+"F0.wireOp",EDGE,"E20");var subQ2=makeQuery(id+"F0.imprint","INTERSECT",VERTEX,{"derivedFrom":[subQ1,subQ0]});Q71=makeQuery(id+"F0.imprint","IMPRINT",FACE,{"disambiguationData":[TD([[makeQuery(id+"F0.imprint","IMPRINT",EDGE,{"disambiguationData":[TD([[subQ2,1.0]])],"derivedFrom":subQ1}),-1.0]])]});}
            var Q72;
            {var subQ3=sQuery(id+"F0.wireOp",EDGE,"E37.0");var subQ6=sQuery(id+"F0.wireOp",EDGE,"E3");var subQ11=makeQuery(id+"F0.imprint","INTERSECT",VERTEX,{"disambiguationData":[OD(0.0)],"derivedFrom":[subQ6,subQ3]});Q72=makeQuery(id+"F0.imprint","IMPRINT",FACE,{"disambiguationData":[TD([[makeQuery(id+"F0.imprint","IMPRINT",EDGE,{"disambiguationData":[TD([[subQ11,-1.0]])],"derivedFrom":subQ6}),1.0]])]});}
            var Q73;
            {var subQ0=sQuery(id+"F0.wireOp",EDGE,"E37.0");var subQ1=sQuery(id+"F0.wireOp",EDGE,"E4");var subQ2=makeQuery(id+"F0.imprint","INTERSECT",VERTEX,{"disambiguationData":[OD(0.0)],"derivedFrom":[subQ1,subQ0]});Q73=makeQuery(id+"F0.imprint","IMPRINT",FACE,{"disambiguationData":[TD([[makeQuery(id+"F0.imprint","IMPRINT",EDGE,{"disambiguationData":[TD([[subQ2,-1.0]])],"derivedFrom":subQ1}),-1.0]])]});}
            var Q74;
            {var subQ0=sQuery(id+"F0.wireOp",EDGE,"E37.0");var subQ1=sQuery(id+"F0.wireOp",EDGE,"E3");var subQ2=makeQuery(id+"F0.imprint","INTERSECT",VERTEX,{"disambiguationData":[OD(0.0)],"derivedFrom":[subQ1,subQ0]});Q74=makeQuery(id+"F0.imprint","IMPRINT",FACE,{"disambiguationData":[TD([[makeQuery(id+"F0.imprint","IMPRINT",EDGE,{"disambiguationData":[TD([[subQ2,-1.0]])],"derivedFrom":subQ1}),-1.0]])]});}
            extrude(context, id + "F1", {"entities" : qUnion([Q0, Q1, Q2, Q3, Q4, Q5, Q6, Q7, Q8, Q9, Q10, Q11, Q12, Q13, Q14, Q15, Q16, Q17, Q18, Q19, Q20, Q21, Q22, Q23, Q24, Q25, Q26, Q27, Q28, Q29, Q30, Q31, Q32, Q33, Q34, Q35, Q36, Q37, Q38, Q39, Q40, Q41, Q42, Q43, Q44, Q45, Q46, Q47, Q48, Q49, Q50, Q51, Q52, Q53, Q54, Q55, Q56, Q57, Q58, Q59, Q60, Q61, Q62, Q63, Q64, Q65, Q66, Q67, Q68, Q69, Q70, Q71, Q72, Q73, Q74]), "depth" : 2 * mm, "offsetDistance" : 25 * mm});
        }
    });
